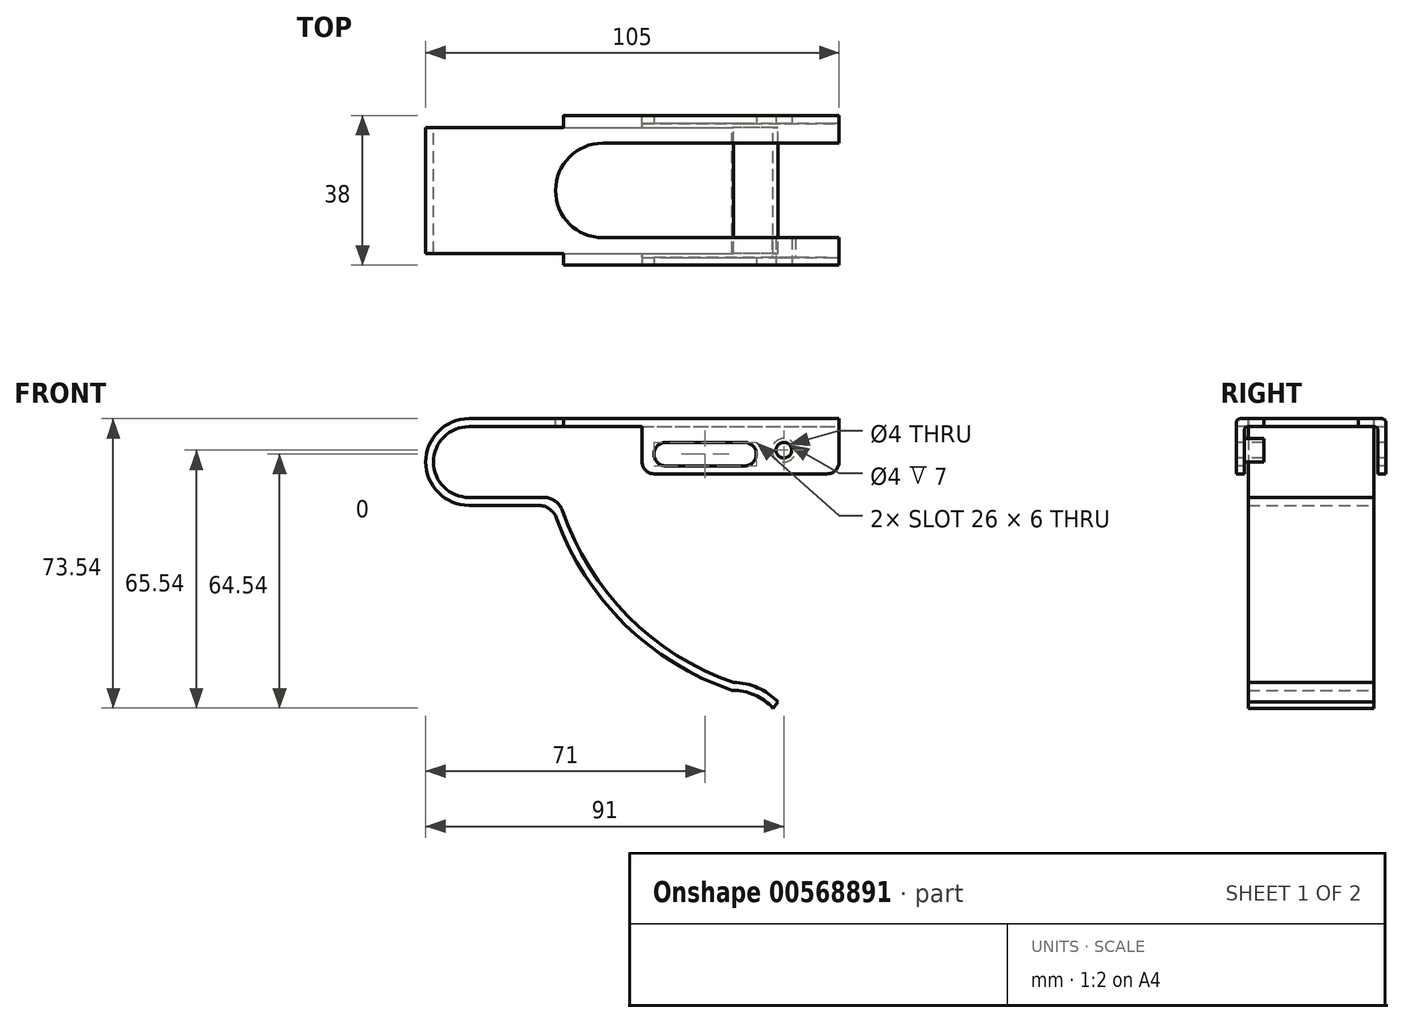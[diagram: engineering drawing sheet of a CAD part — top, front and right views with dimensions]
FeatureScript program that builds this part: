
annotation { "Feature Type Name" : "Feature", "Feature Type Description" : "" }
export const myFeature = defineFeature(function(context is Context, id is Id, definition is map)
    precondition{}
    {
        {
            var Q0;
            Q0=qCreatedBy(makeId("Front.planeOp"),FACE);
            var sketch = newSketch(context, id + "F0", { "sketchPlane" : qUnion([Q0])});
            skArc(sketch, "E0", {"start": v(0, 11) * mm, "mid": v(-11, 0) * mm, "end": v(0, -11) * mm});
            skLineSegment(sketch, "E1", {"start": v(0, 11) * mm, "end": v(94, 11) * mm});
            skLineSegment(sketch, "E2", {"start": v(0, -11) * mm, "end": v(17.58, -11) * mm});
            skArc(sketch, "E3", {"start": v(22.28, -14.3) * mm, "mid": v(39.57, -41.22) * mm, "end": v(66.81, -58) * mm});
            skArc(sketch, "E4", {"start": v(77.24, -62.54) * mm, "mid": v(72.51, -59.16) * mm, "end": v(66.81, -58) * mm});
            skPoint(sketch, "E5.visualSharp", {"position": v(21.18, -11) * mm});
            skArc(sketch, "E5.filletArc", {"start": v(22.28, -14.3) * mm, "mid": v(20.45, -11.9) * mm, "end": v(17.58, -11) * mm});
            skArc(sketch, "E6.0", {"start": v(78.54, -61) * mm, "mid": v(73.35, -57.35) * mm, "end": v(67.15, -56) * mm});
            skLineSegment(sketch, "E6.1", {"start": v(0, 9) * mm, "end": v(94, 9) * mm});
            skArc(sketch, "E6.2", {"start": v(0, 9) * mm, "mid": v(-9, 0) * mm, "end": v(0, -9) * mm});
            skLineSegment(sketch, "E6.3", {"start": v(0, -9) * mm, "end": v(19, -9) * mm});
            skArc(sketch, "E6.4", {"start": v(23.73, -12.39) * mm, "mid": v(40.4, -39.22) * mm, "end": v(67.15, -56) * mm});
            skPoint(sketch, "E7.visualSharp", {"position": v(22.67, -9) * mm});
            skArc(sketch, "E7.filletArc", {"start": v(23.73, -12.39) * mm, "mid": v(21.91, -9.93) * mm, "end": v(19, -9) * mm});
            skLineSegment(sketch, "E8", {"start": v(77.24, -62.54) * mm, "end": v(78.54, -61) * mm});
            skLineSegment(sketch, "E9", {"start": v(94, 9) * mm, "end": v(94, 11) * mm});
            skSolve(sketch);
        }
        {
            var Q0;
            Q0 = qSketchRegion(id + "F0", true);
            extrude(context, id + "F1", {"entities" : qUnion([Q0]), "depth" : 16 * mm, "offsetDistance" : 25 * mm});
        }
        {
            var Q0;
            Q0=makeQuery(id+"F1.opExtrude","SWEPT_FACE",FACE,{"disambiguationData":[OSD([sQuery(id+"F0.wireOp",EDGE,"E1")])]});
            var sketch = newSketch(context, id + "F2", { "sketchPlane" : qUnion([Q0])});
            skLineSegment(sketch, "E10.bottom", {"start": v(94, -16) * mm, "end": v(24, -16) * mm});
            skLineSegment(sketch, "E10.top", {"start": v(94, -19) * mm, "end": v(24, -19) * mm});
            skLineSegment(sketch, "E10.left", {"start": v(94, -16) * mm, "end": v(94, -19) * mm});
            skLineSegment(sketch, "E10.right", {"start": v(24, -16) * mm, "end": v(24, -19) * mm});
            skSolve(sketch);
        }
        {
            var Q0;
            Q0=makeQuery(id+"F2.imprint","IMPRINT",FACE,{"disambiguationData":[TD([[makeQuery(id+"F2.imprint","IMPRINT",EDGE,{"derivedFrom":sQuery(id+"F2.wireOp",EDGE,"E10.bottom")}),-1.0]])]});
            extrude(context, id + "F3", {"entities" : qUnion([Q0]), "operationType" : NewBodyOperationType.ADD, "oppositeDirection" : true, "depth" : 2 * mm, "offsetDistance" : 25 * mm});
        }
        {
            var Q0;
            Q0=makeQuery(id+"F3.opExtrude","SWEPT_FACE",FACE,{"disambiguationData":[OSD([sQuery(id+"F2.wireOp",EDGE,"E10.top")])]});
            var sketch = newSketch(context, id + "F4", { "sketchPlane" : qUnion([Q0])});
            skLineSegment(sketch, "E11.bottom", {"start": v(94, 11) * mm, "end": v(44, 11) * mm});
            skLineSegment(sketch, "E11.top", {"start": v(94, -3) * mm, "end": v(44, -3) * mm});
            skLineSegment(sketch, "E11.left", {"start": v(94, 11) * mm, "end": v(94, -3) * mm});
            skLineSegment(sketch, "E11.right", {"start": v(44, 11) * mm, "end": v(44, -3) * mm});
            skSolve(sketch);
        }
        {
            var Q0;
            Q0 = qSketchRegion(id + "F4", true);
            extrude(context, id + "F5", {"entities" : qUnion([Q0]), "operationType" : NewBodyOperationType.ADD, "oppositeDirection" : true, "depth" : 2 * mm, "offsetDistance" : 25 * mm});
        }
        {
            var Q0;
            Q0=makeQuery(id+"F3.opExtrude","CAP_EDGE",EDGE,{"disambiguationData":[OSD([sQuery(id+"F2.wireOp",EDGE,"E10.top")])],"isStart":true});
            var Q1;
            Q1=makeQuery(id+"F5.boolean.opBoolean","INTERSECT",EDGE,{"derivedFrom":[makeQuery(id+"F3.boolean.opBoolean","MERGE",FACE,{"derivedFrom":[makeQuery(id+"F1.opExtrude","SWEPT_FACE",FACE,{"disambiguationData":[OSD([sQuery(id+"F0.wireOp",EDGE,"E6.1")])]}),makeQuery(id+"F3.opExtrude","CAP_FACE",FACE,{"disambiguationData":[OSD([sQuery(id+"F2.wireOp",EDGE,"E10.bottom"),sQuery(id+"F2.wireOp",EDGE,"E10.top"),sQuery(id+"F2.wireOp",EDGE,"E10.left"),sQuery(id+"F2.wireOp",EDGE,"E10.right")])],"isStart":false})]}),makeQuery(id+"F5.opExtrude","CAP_FACE",FACE,{"disambiguationData":[OSD([sQuery(id+"F4.wireOp",EDGE,"E11.bottom"),sQuery(id+"F4.wireOp",EDGE,"E11.top"),sQuery(id+"F4.wireOp",EDGE,"E11.left"),sQuery(id+"F4.wireOp",EDGE,"E11.right")])],"isStart":false})]});
            fillet(context, id + "F6", {"entities" : qUnion([Q0, Q1]), "radius" : 1 * mm, "allowEdgeOverflow" : false});
        }
        {
            var Q0;
            Q0=makeQuery(id+"F1.opExtrude","SWEPT_BODY",BODY,{"disambiguationData":[OSD([sQuery(id+"F0.wireOp",EDGE,"E0"),sQuery(id+"F0.wireOp",EDGE,"E1"),sQuery(id+"F0.wireOp",EDGE,"E2"),sQuery(id+"F0.wireOp",EDGE,"E3"),sQuery(id+"F0.wireOp",EDGE,"E4"),sQuery(id+"F0.wireOp",EDGE,"E5.filletArc"),sQuery(id+"F0.wireOp",EDGE,"E6.0"),sQuery(id+"F0.wireOp",EDGE,"E6.1"),sQuery(id+"F0.wireOp",EDGE,"E6.2"),sQuery(id+"F0.wireOp",EDGE,"E6.3"),sQuery(id+"F0.wireOp",EDGE,"E6.4"),sQuery(id+"F0.wireOp",EDGE,"E7.filletArc"),sQuery(id+"F0.wireOp",EDGE,"E8"),sQuery(id+"F0.wireOp",EDGE,"E9")])]});
            var Q1;
            Q1=qCreatedBy(makeId("Front.planeOp"),FACE);
            mirror(context, id + "F7", {"operationType" : NewBodyOperationType.ADD, "entities" : qUnion([Q0]), "mirrorPlane" : qUnion([Q1])});
        }
        {
            var Q0;
            {var subQ0=makeQuery(id+"F3.boolean.opBoolean","MERGE",FACE,{"derivedFrom":[makeQuery(id+"F1.opExtrude","SWEPT_FACE",FACE,{"disambiguationData":[OSD([sQuery(id+"F0.wireOp",EDGE,"E1")])]}),makeQuery(id+"F3.opExtrude","CAP_FACE",FACE,{"disambiguationData":[OSD([sQuery(id+"F2.wireOp",EDGE,"E10.bottom"),sQuery(id+"F2.wireOp",EDGE,"E10.top"),sQuery(id+"F2.wireOp",EDGE,"E10.left"),sQuery(id+"F2.wireOp",EDGE,"E10.right")])],"isStart":true})]});Q0=makeQuery(id+"F7.boolean.opBoolean","MERGE",FACE,{"derivedFrom":[subQ0,makeQuery(id+"F7.opPattern","COPY",FACE,{"derivedFrom":subQ0,"instanceName":"1"})]});}
            var sketch = newSketch(context, id + "F8", { "sketchPlane" : qUnion([Q0])});
            skArc(sketch, "E12", {"start": v(34, 12) * mm, "mid": v(22, 0) * mm, "end": v(34, -12) * mm});
            skLineSegment(sketch, "E13", {"start": v(34, 12) * mm, "end": v(94, 12) * mm});
            skLineSegment(sketch, "E14", {"start": v(34, -12) * mm, "end": v(94, -12) * mm});
            skLineSegment(sketch, "E15", {"start": v(94, -12) * mm, "end": v(94, 12) * mm});
            skSolve(sketch);
        }
        {
            var Q0;
            Q0 = qSketchRegion(id + "F8", true);
            extrude(context, id + "F9", {"entities" : qUnion([Q0]), "operationType" : NewBodyOperationType.REMOVE, "oppositeDirection" : true, "depth" : 2 * mm, "offsetDistance" : 25 * mm});
        }
        {
            var Q0;
            Q0=makeQuery(id+"F5.boolean.opBoolean","MERGE",FACE,{"derivedFrom":[makeQuery(id+"F3.opExtrude","SWEPT_FACE",FACE,{"disambiguationData":[OSD([sQuery(id+"F2.wireOp",EDGE,"E10.top")])]}),makeQuery(id+"F5.opExtrude","CAP_FACE",FACE,{"disambiguationData":[OSD([sQuery(id+"F4.wireOp",EDGE,"E11.bottom"),sQuery(id+"F4.wireOp",EDGE,"E11.top"),sQuery(id+"F4.wireOp",EDGE,"E11.left"),sQuery(id+"F4.wireOp",EDGE,"E11.right")])],"isStart":true})]});
            var sketch = newSketch(context, id + "F10", { "sketchPlane" : qUnion([Q0])});
            skLineSegment(sketch, "E16", {"start": v(50, 2) * mm, "end": v(70, 2) * mm});
            skArc(sketch, "E17.0.startCap", {"start": v(50, -1) * mm, "mid": v(47, 2) * mm, "end": v(50, 5) * mm});
            skArc(sketch, "E17.0.endCap", {"start": v(70, 5) * mm, "mid": v(73, 2) * mm, "end": v(70, -1) * mm});
            skLineSegment(sketch, "E17.0.left", {"start": v(50, 5) * mm, "end": v(70, 5) * mm});
            skLineSegment(sketch, "E17.0.right", {"start": v(50, -1) * mm, "end": v(70, -1) * mm});
            skSolve(sketch);
        }
        {
            var Q0;
            Q0 = qSketchRegion(id + "F10", true);
            extrude(context, id + "F11", {"entities" : qUnion([Q0]), "operationType" : NewBodyOperationType.REMOVE, "endBound" : BoundingType.THROUGH_ALL, "oppositeDirection" : true, "depth" : 25 * mm, "offsetDistance" : 25 * mm});
        }
        {
            var Q0;
            Q0=makeQuery(id+"F5.boolean.opBoolean","MERGE",FACE,{"derivedFrom":[makeQuery(id+"F3.opExtrude","SWEPT_FACE",FACE,{"disambiguationData":[OSD([sQuery(id+"F2.wireOp",EDGE,"E10.top")])]}),makeQuery(id+"F5.opExtrude","CAP_FACE",FACE,{"disambiguationData":[OSD([sQuery(id+"F4.wireOp",EDGE,"E11.bottom"),sQuery(id+"F4.wireOp",EDGE,"E11.top"),sQuery(id+"F4.wireOp",EDGE,"E11.left"),sQuery(id+"F4.wireOp",EDGE,"E11.right")])],"isStart":true})]});
            var sketch = newSketch(context, id + "F12", { "sketchPlane" : qUnion([Q0])});
            skPoint(sketch, "E18", {"position": v(80, 3) * mm});
            skSolve(sketch);
        }
        {
            var Q0;
            Q0=sQuery(id+"F12.wireOp",VERTEX,"E18");
            var Q1;
            Q1=makeQuery(id+"F1.opExtrude","SWEPT_BODY",BODY,{"disambiguationData":[OSD([sQuery(id+"F0.wireOp",EDGE,"E0"),sQuery(id+"F0.wireOp",EDGE,"E1"),sQuery(id+"F0.wireOp",EDGE,"E2"),sQuery(id+"F0.wireOp",EDGE,"E3"),sQuery(id+"F0.wireOp",EDGE,"E4"),sQuery(id+"F0.wireOp",EDGE,"E5.filletArc"),sQuery(id+"F0.wireOp",EDGE,"E6.0"),sQuery(id+"F0.wireOp",EDGE,"E6.1"),sQuery(id+"F0.wireOp",EDGE,"E6.2"),sQuery(id+"F0.wireOp",EDGE,"E6.3"),sQuery(id+"F0.wireOp",EDGE,"E6.4"),sQuery(id+"F0.wireOp",EDGE,"E7.filletArc"),sQuery(id+"F0.wireOp",EDGE,"E8"),sQuery(id+"F0.wireOp",EDGE,"E9")])]});
            hole(context, id + "F13", {"style" : HoleStyle.SIMPLE, "endStyle" : HoleEndStyle.THROUGH, "holeDiameter" : 4 * mm, "majorDiameter" : 5 * mm, "isTappedThrough" : true, "tappedDepth" : 12 * mm, "tapClearance" : 3, "locations" : qUnion([Q0]), "scope" : qUnion([Q1])});
        }
        {
            var Q0;
            Q0=makeQuery(id+"F5.opExtrude","CAP_FACE",FACE,{"disambiguationData":[OSD([sQuery(id+"F4.wireOp",EDGE,"E11.bottom"),sQuery(id+"F4.wireOp",EDGE,"E11.top"),sQuery(id+"F4.wireOp",EDGE,"E11.left"),sQuery(id+"F4.wireOp",EDGE,"E11.right")])],"isStart":false});
            var sketch = newSketch(context, id + "F14", { "sketchPlane" : qUnion([Q0])});
            skCircle(sketch, "E19.0", {"center": v(-80, 3) * mm, "radius": 2 * mm});
            skCircle(sketch, "E20.0", {"center": v(-80, 3) * mm, "radius": 3 * mm});
            skSolve(sketch);
        }
        {
            var Q0;
            Q0 = qSketchRegion(id + "F14", true);
            extrude(context, id + "F15", {"entities" : qUnion([Q0]), "operationType" : NewBodyOperationType.ADD, "depth" : 5 * mm, "offsetDistance" : 25 * mm});
        }
        {
            var Q0;
            Q0=makeQuery(id+"F5.opExtrude","SWEPT_EDGE",EDGE,{"disambiguationData":[OSD([sQuery(id+"F4.wireOp",EDGE,"E11.top"),sQuery(id+"F4.wireOp",EDGE,"E11.right")])]});
            var Q1;
            Q1=makeQuery(id+"F5.opExtrude","SWEPT_EDGE",EDGE,{"disambiguationData":[OSD([sQuery(id+"F4.wireOp",EDGE,"E11.top"),sQuery(id+"F4.wireOp",EDGE,"E11.left")])]});
            var Q2;
            Q2=makeQuery(id+"F7.opPattern","COPY",EDGE,{"derivedFrom":makeQuery(id+"F5.opExtrude","SWEPT_EDGE",EDGE,{"disambiguationData":[OSD([sQuery(id+"F4.wireOp",EDGE,"E11.top"),sQuery(id+"F4.wireOp",EDGE,"E11.right")])]}),"instanceName":"1"});
            var Q3;
            Q3=makeQuery(id+"F7.opPattern","COPY",EDGE,{"derivedFrom":makeQuery(id+"F5.opExtrude","SWEPT_EDGE",EDGE,{"disambiguationData":[OSD([sQuery(id+"F4.wireOp",EDGE,"E11.top"),sQuery(id+"F4.wireOp",EDGE,"E11.left")])]}),"instanceName":"1"});
            fillet(context, id + "F16", {"entities" : qUnion([Q0, Q1, Q2, Q3]), "radius" : 3 * mm, "tangentPropagation" : true, "allowEdgeOverflow" : false});
        }
    });
